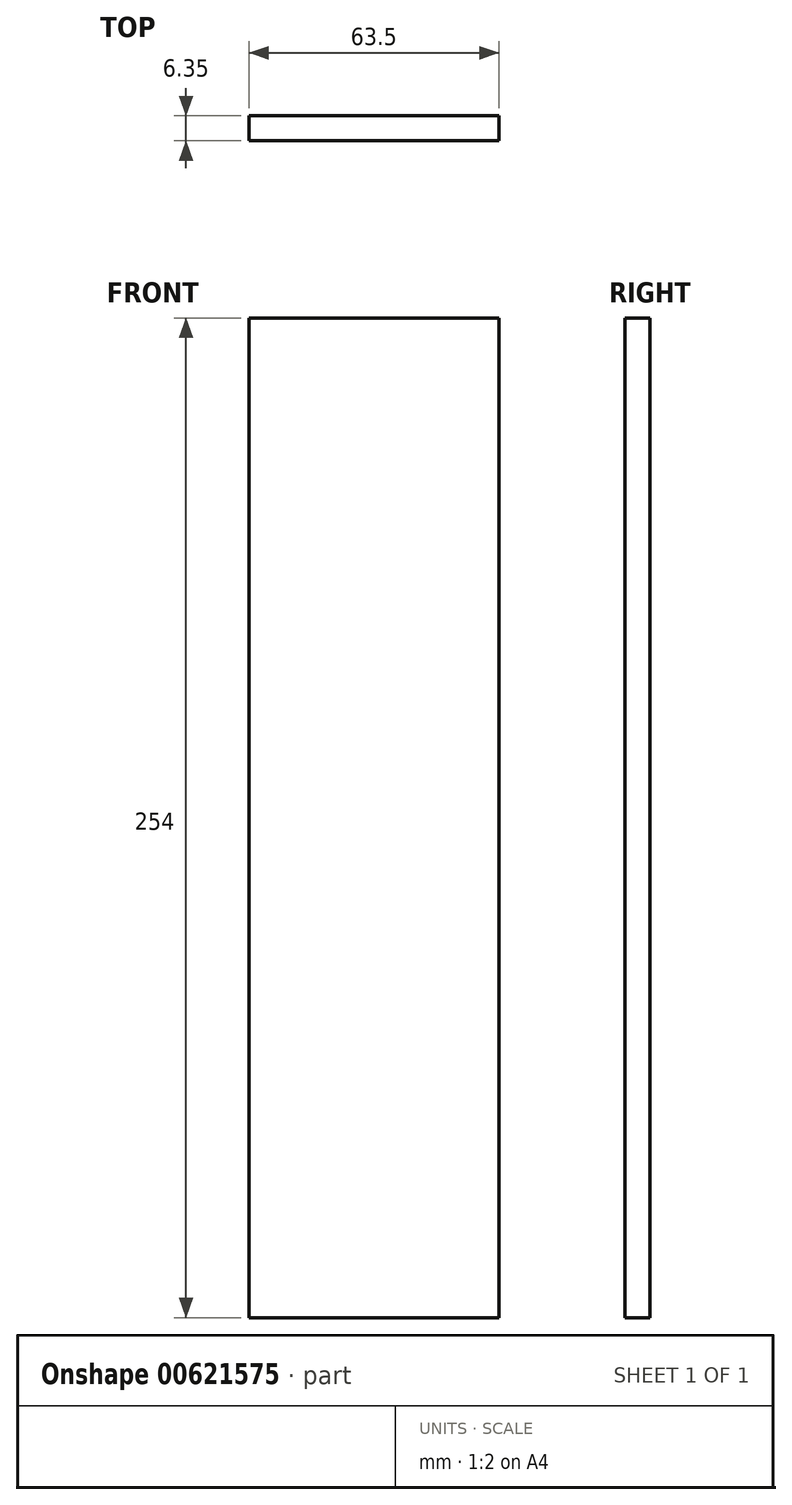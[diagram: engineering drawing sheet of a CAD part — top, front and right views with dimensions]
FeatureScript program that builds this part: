
annotation { "Feature Type Name" : "Feature", "Feature Type Description" : "" }
export const myFeature = defineFeature(function(context is Context, id is Id, definition is map)
    precondition{}
    {
        {
            var Q0;
            Q0=qCreatedBy(makeId("Front.planeOp"),FACE);
            var sketch = newSketch(context, id + "F0", { "sketchPlane" : qUnion([Q0])});
            skLineSegment(sketch, "E0.bottom", {"start": v(31.75, 127) * mm, "end": v(-31.75, 127) * mm});
            skLineSegment(sketch, "E0.top", {"start": v(31.75, -127) * mm, "end": v(-31.75, -127) * mm});
            skLineSegment(sketch, "E0.left", {"start": v(31.75, 127) * mm, "end": v(31.75, -127) * mm});
            skLineSegment(sketch, "E0.right", {"start": v(-31.75, 127) * mm, "end": v(-31.75, -127) * mm});
            skPoint(sketch, "E0.middle", {"position": v(0, 0) * mm});
            skSolve(sketch);
        }
        {
            var Q0;
            Q0=makeQuery(id+"F0.imprint","IMPRINT",FACE,{"disambiguationData":[TD([[makeQuery(id+"F0.imprint","IMPRINT",EDGE,{"derivedFrom":sQuery(id+"F0.wireOp",EDGE,"E0.bottom")}),1.0]])]});
            extrude(context, id + "F1", {"entities" : qUnion([Q0]), "depth" : 6.35 * mm, "offsetDistance" : 25.4 * mm});
        }
    });
